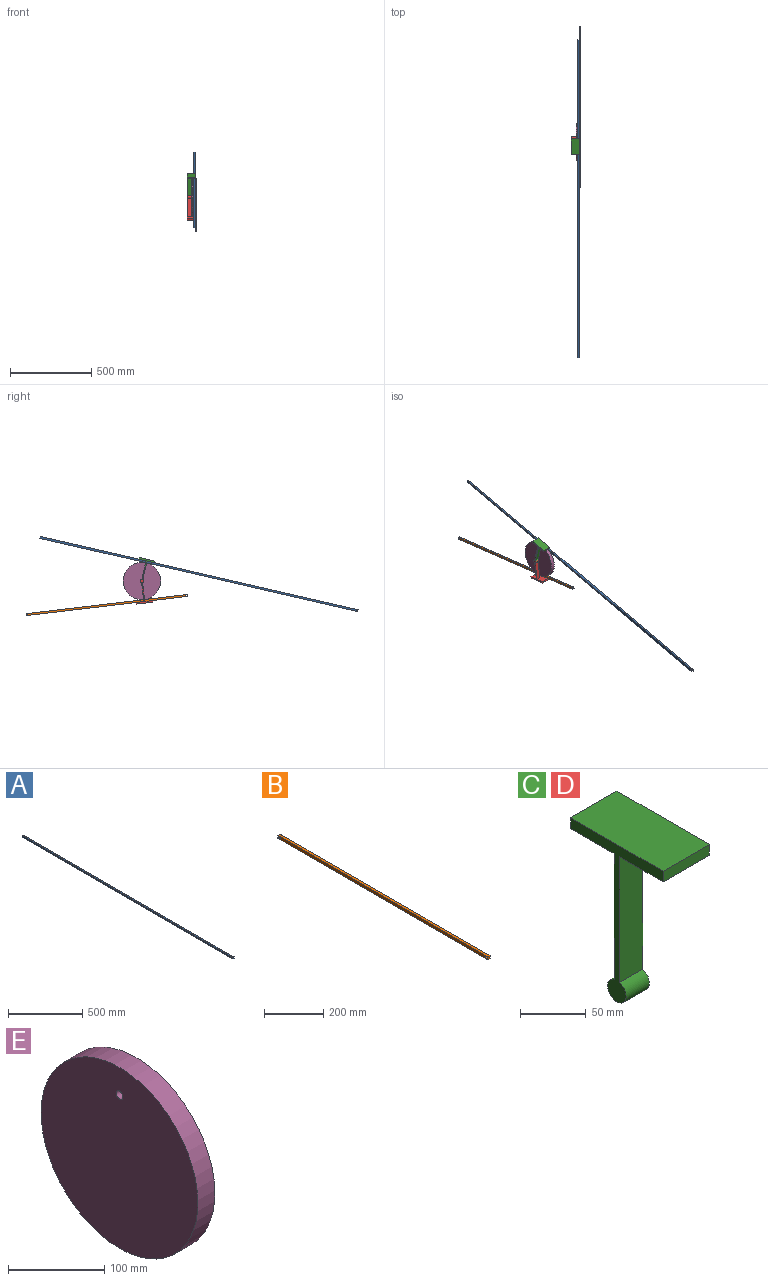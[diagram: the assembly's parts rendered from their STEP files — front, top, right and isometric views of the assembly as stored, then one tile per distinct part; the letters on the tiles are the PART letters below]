
ASSEMBLY  parts=5 mates=6
PART A: 7 faces, bbox 10x2006x12 mm
  f0: plane 12x10mm, normal (0,1,0), area 120mm2, adj f1,f3,f5,f6
  f1: plane 2006x10mm, normal (0,0,1), area 20060mm2, adj f0,f2,f5,f6
  f2: plane 12x10mm, normal (0,-1,0), area 120mm2, adj f1,f3,f5,f6
  f3: plane 2006x10mm, normal (0,0,-1), area 20060mm2, adj f0,f2,f5,f6
  f4: cylinder r=5mm len=10mm, axis (-1,0,0), area 314.2mm2, adj f5,f6
  f5: plane 2006x12mm, normal (1,0,0), area 23993.5mm2, adj f0,f1,f2,f3,f4
  f6: plane 2006x12mm, normal (-1,0,0), area 23993.5mm2, adj f0,f1,f2,f3,f4
PART B: 8 faces, bbox 10x1000x12 mm
  f0: plane 12x10mm, normal (0,1,0), area 120mm2, adj f1,f4,f6,f7
  f1: plane 1000x10mm, normal (0,0,1), area 10000mm2, adj f0,f2,f6,f7
  f2: plane 12x10mm, normal (0,-1,0), area 120mm2, adj f1,f4,f6,f7
  f3: cylinder r=5mm len=10mm, axis (-1,0,0), area 314.2mm2, adj f6,f7
  f4: plane 1000x10mm, normal (0,0,-1), area 10000mm2, adj f0,f2,f6,f7
  f5: cylinder r=5mm len=10mm, axis (-1,0,0), area 314.2mm2, adj f6,f7
  f6: plane 1000x12mm, normal (1,0,0), area 11842.9mm2, adj f0,f1,f2,f3,f4,f5
  f7: plane 1000x12mm, normal (-1,0,0), area 11842.9mm2, adj f0,f1,f2,f3,f4,f5
PART C: 10 faces, bbox 50x100x147 mm
  f0: plane 137x20mm, normal (1,0,0), area 1031.9mm2, adj f4,f5,f6,f7
  f1: plane 50x10mm, normal (0,1,0), area 500mm2, adj f2,f4,f8,f9
  f2: plane 100x50mm, normal (0,0,1), area 5000mm2, adj f1,f3,f8,f9
  f3: plane 50x10mm, normal (0,-1,0), area 500mm2, adj f2,f4,f8,f9
  f4: plane 100x50mm, normal (0,0,-1), area 4846.8mm2, adj f0,f1,f3,f5,f7,f8,f9
  f5: plane 117.48x25mm, normal (0,-1,0), area 2937mm2, adj f0,f4,f6,f8
  f6: cylinder r=10mm len=25mm, axis (-1,0,0), area 1415.1mm2, adj f0,f5,f7,f8
  f7: plane 117.48x25mm, normal (0,1,0), area 2937mm2, adj f0,f4,f6,f8
  f8: plane 147x100mm, normal (-1,0,0), area 2031.9mm2, adj f1,f2,f3,f4,f5,f6,f7
  f9: plane 100x10mm, normal (1,0,0), area 1000mm2, adj f1,f2,f3,f4
PART D: same geometry as C
PART E: 4 faces, bbox 25x230x230 mm
  f0: cylinder r=5mm len=25mm, axis (-1,0,0), area 785.4mm2, adj f2,f3
  f1: cylinder r=115mm len=230mm, axis (-1,0,0), area 18064.2mm2, adj f2,f3
  f2: plane 230x230mm, normal (1,0,0), area 41469mm2, adj f0,f1
  f3: plane 230x230mm, normal (-1,0,0), area 41469mm2, adj f0,f1
PLACE A rot(axis=(1,0,0),13deg) t=(-76.79,-1341.4,-28.76)mm
PLACE B rot(axis=(0,0.06,1),180deg) t=(-56.79,687.34,-53.97)mm
PLACE C rot(axis=(1,0,0),13deg) t=(-116.79,-19.24,151.94)mm fixed
PLACE D rot(axis=(1,0,0),173.2deg) t=(-116.79,-19.24,151.94)mm
PLACE E rot(axis=(1,0,0),174.6deg) t=(-86.79,-19.24,151.94)mm
MATE planar A.f5 <-> C.f9  axis (1,0,0) through (-66.79,-366.72,195.99)mm
MATE planar B.f4 <-> D.f4  axis (0,-0.12,-0.99) through (-61.79,196.09,-1.57)mm
MATE planar A.f1 <-> C.f4  axis (0,-0.22,0.97) through (-71.79,-371.25,201.1)mm
MATE revolute C.f6 <-> E.f1  axis (-1,0,0) through (-91.79,-19.24,151.94)mm
MATE revolute D.f6 <-> C.f6  axis (-1,0,0) through (-116.79,-19.24,151.94)mm
MATE planar B.f6 <-> D.f9  axis (-1,0,0) through (-66.79,196.8,4.39)mm
